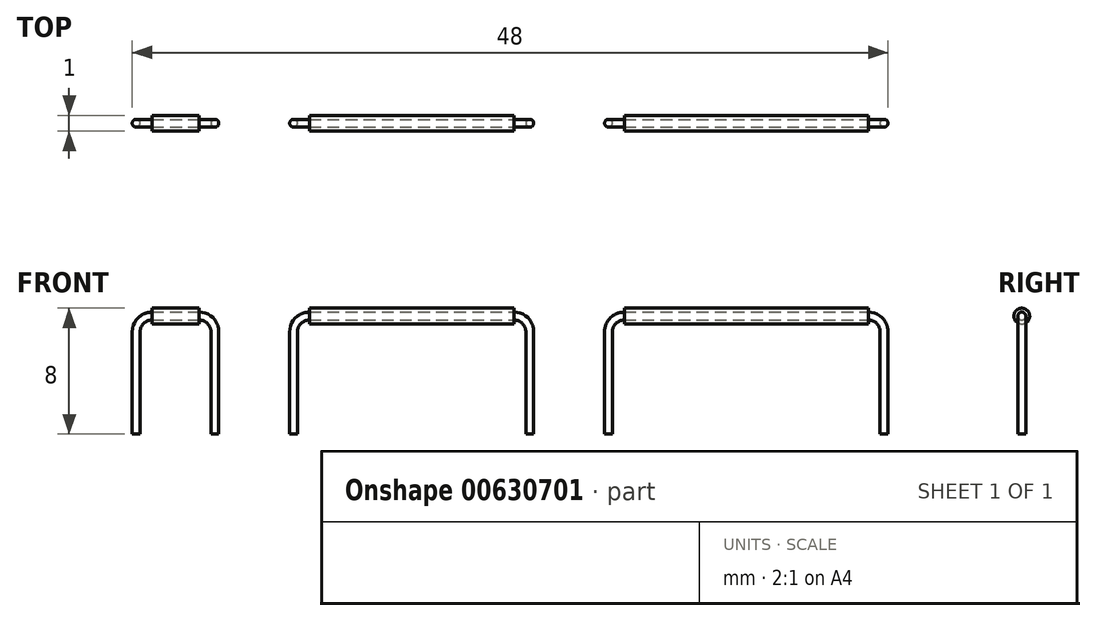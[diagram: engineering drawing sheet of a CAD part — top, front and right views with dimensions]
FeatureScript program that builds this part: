
annotation { "Feature Type Name" : "Feature", "Feature Type Description" : "" }
export const myFeature = defineFeature(function(context is Context, id is Id, definition is map)
    precondition{}
    {
        {
            var Q0;
            Q0=qCreatedBy(makeId("Front.planeOp"),FACE);
            var sketch = newSketch(context, id + "F0", { "sketchPlane" : qUnion([Q0])});
            skLineSegment(sketch, "E0", {"start": v(5, 0) * mm, "end": v(5, 6.5) * mm});
            skLineSegment(sketch, "E1", {"start": v(6, 7.5) * mm, "end": v(9, 7.5) * mm});
            skLineSegment(sketch, "E2", {"start": v(10, 6.5) * mm, "end": v(10, 0) * mm});
            skPoint(sketch, "E3.visualSharp", {"position": v(10, 7.5) * mm});
            skArc(sketch, "E3.filletArc", {"start": v(10, 6.5) * mm, "mid": v(9.7, 7.2) * mm, "end": v(9, 7.5) * mm});
            skPoint(sketch, "E4.visualSharp", {"position": v(5, 7.5) * mm});
            skArc(sketch, "E4.filletArc", {"start": v(6, 7.5) * mm, "mid": v(5.3, 7.2) * mm, "end": v(5, 6.5) * mm});
            skSolve(sketch);
        }
        {
            var Q0;
            Q0=qCreatedBy(makeId("Top.planeOp"),FACE);
            var sketch = newSketch(context, id + "F1", { "sketchPlane" : qUnion([Q0])});
            skPoint(sketch, "E5.0", {"position": v(5, 0) * mm});
            skCircle(sketch, "E6", {"center": v(5, 0) * mm, "radius": 0.25 * mm});
            skSolve(sketch);
        }
        {
            var Q0;
            Q0 = qSketchRegion(id + "F1", true);
            var Q1;
            Q1 = qConstructionFilter(qBodyType(qCreatedBy(id + "F0" ,EDGE), BodyType.WIRE), ConstructionObject.NO);
            sweep(context, id + "F2", {"profiles" : qUnion([Q0]), "path" : qUnion([Q1])});
        }
        {
            var Q0;
            Q0=qCreatedBy(makeId("Front.planeOp"),FACE);
            var sketch = newSketch(context, id + "F3", { "sketchPlane" : qUnion([Q0])});
            skLineSegment(sketch, "E7", {"start": v(15, 0) * mm, "end": v(15, 6.5) * mm});
            skLineSegment(sketch, "E8", {"start": v(16, 7.5) * mm, "end": v(29, 7.5) * mm});
            skLineSegment(sketch, "E9", {"start": v(30, 6.5) * mm, "end": v(30, 0) * mm});
            skPoint(sketch, "E10.visualSharp", {"position": v(30, 7.5) * mm});
            skArc(sketch, "E10.filletArc", {"start": v(30, 6.5) * mm, "mid": v(29.7, 7.2) * mm, "end": v(29, 7.5) * mm});
            skPoint(sketch, "E11.visualSharp", {"position": v(15, 7.5) * mm});
            skArc(sketch, "E11.filletArc", {"start": v(16, 7.5) * mm, "mid": v(15.3, 7.2) * mm, "end": v(15, 6.5) * mm});
            skLineSegment(sketch, "E12", {"start": v(35, 0) * mm, "end": v(35, 6.5) * mm});
            skLineSegment(sketch, "E13", {"start": v(36, 7.5) * mm, "end": v(51.5, 7.5) * mm});
            skLineSegment(sketch, "E14", {"start": v(52.5, 6.5) * mm, "end": v(52.5, 0) * mm});
            skPoint(sketch, "E15.visualSharp", {"position": v(52.5, 7.5) * mm});
            skArc(sketch, "E15.filletArc", {"start": v(52.5, 6.5) * mm, "mid": v(52.2, 7.2) * mm, "end": v(51.5, 7.5) * mm});
            skPoint(sketch, "E16.visualSharp", {"position": v(35, 7.5) * mm});
            skArc(sketch, "E16.filletArc", {"start": v(36, 7.5) * mm, "mid": v(35.3, 7.2) * mm, "end": v(35, 6.5) * mm});
            skSolve(sketch);
        }
        {
            var Q0;
            Q0=qCreatedBy(makeId("Top.planeOp"),FACE);
            var sketch = newSketch(context, id + "F4", { "sketchPlane" : qUnion([Q0])});
            skCircle(sketch, "E17", {"center": v(15, 0) * mm, "radius": 0.25 * mm});
            skCircle(sketch, "E18", {"center": v(35, 0) * mm, "radius": 0.25 * mm});
            skSolve(sketch);
        }
        {
            var Q0;
            Q0=makeQuery(id+"F4.imprint","IMPRINT",FACE,{"disambiguationData":[TD([[makeQuery(id+"F4.imprint","IMPRINT",EDGE,{"derivedFrom":sQuery(id+"F4.wireOp",EDGE,"E17")}),1.0]])]});
            var Q1;
            Q1=sQuery(id+"F3.wireOp",EDGE,"E8");
            var Q2;
            Q2=sQuery(id+"F3.wireOp",EDGE,"E10.filletArc");
            var Q3;
            Q3=sQuery(id+"F3.wireOp",EDGE,"E7");
            var Q4;
            Q4=sQuery(id+"F3.wireOp",EDGE,"E9");
            var Q5;
            Q5=sQuery(id+"F3.wireOp",EDGE,"E11.filletArc");
            sweep(context, id + "F5", {"profiles" : qUnion([Q0]), "path" : qUnion([Q1, Q2, Q3, Q4, Q5])});
        }
        {
            var Q0;
            Q0=makeQuery(id+"F4.imprint","IMPRINT",FACE,{"disambiguationData":[TD([[makeQuery(id+"F4.imprint","IMPRINT",EDGE,{"derivedFrom":sQuery(id+"F4.wireOp",EDGE,"E18")}),1.0]])]});
            var Q1;
            Q1=sQuery(id+"F3.wireOp",EDGE,"E16.filletArc");
            var Q2;
            Q2=sQuery(id+"F3.wireOp",EDGE,"E13");
            var Q3;
            Q3=sQuery(id+"F3.wireOp",EDGE,"E15.filletArc");
            var Q4;
            Q4=sQuery(id+"F3.wireOp",EDGE,"E14");
            var Q5;
            Q5=sQuery(id+"F3.wireOp",EDGE,"E12");
            sweep(context, id + "F6", {"profiles" : qUnion([Q0]), "path" : qUnion([Q1, Q2, Q3, Q4, Q5])});
        }
        {
            var Q0;
            Q0=qCreatedBy(makeId("Front.planeOp"),FACE);
            var sketch = newSketch(context, id + "F7", { "sketchPlane" : qUnion([Q0])});
            skLineSegment(sketch, "E19", {"start": v(1.7, 7.5) * mm, "end": v(55.74, 7.5) * mm, "construction": true});
            skLineSegment(sketch, "E20.0", {"start": v(6, 7.75) * mm, "end": v(6, 7.25) * mm});
            skLineSegment(sketch, "E21.0", {"start": v(9, 7.75) * mm, "end": v(9, 7.25) * mm});
            skLineSegment(sketch, "E22.0", {"start": v(16, 7.5) * mm, "end": v(29, 7.5) * mm});
            skLineSegment(sketch, "E23.0", {"start": v(36, 7.5) * mm, "end": v(51.5, 7.5) * mm});
            skLineSegment(sketch, "E24.top", {"start": v(36, 8) * mm, "end": v(51.5, 8) * mm});
            skLineSegment(sketch, "E24.left", {"start": v(36, 7.5) * mm, "end": v(36, 8) * mm});
            skLineSegment(sketch, "E24.right", {"start": v(51.5, 7.5) * mm, "end": v(51.5, 8) * mm});
            skLineSegment(sketch, "E25.bottom", {"start": v(29, 7.5) * mm, "end": v(16, 7.5) * mm});
            skLineSegment(sketch, "E25.top", {"start": v(29, 8) * mm, "end": v(16, 8) * mm});
            skLineSegment(sketch, "E25.left", {"start": v(29, 7.5) * mm, "end": v(29, 8) * mm});
            skLineSegment(sketch, "E25.right", {"start": v(16, 7.5) * mm, "end": v(16, 8) * mm});
            skLineSegment(sketch, "E26.bottom", {"start": v(9, 7.5) * mm, "end": v(6, 7.5) * mm});
            skLineSegment(sketch, "E26.top", {"start": v(9, 8) * mm, "end": v(6, 8) * mm});
            skLineSegment(sketch, "E26.left", {"start": v(9, 7.5) * mm, "end": v(9, 8) * mm});
            skLineSegment(sketch, "E26.right", {"start": v(6, 7.5) * mm, "end": v(6, 8) * mm});
            skSolve(sketch);
        }
        {
            var Q0;
            Q0 = qSketchRegion(id + "F7", true);
            var Q1;
            Q1=sQuery(id+"F7.wireOp",EDGE,"E19");
            revolve(context, id + "F8", {"entities" : qUnion([Q0]), "axis" : qUnion([Q1]), "revolveType" : RevolveType.FULL});
        }
    });
